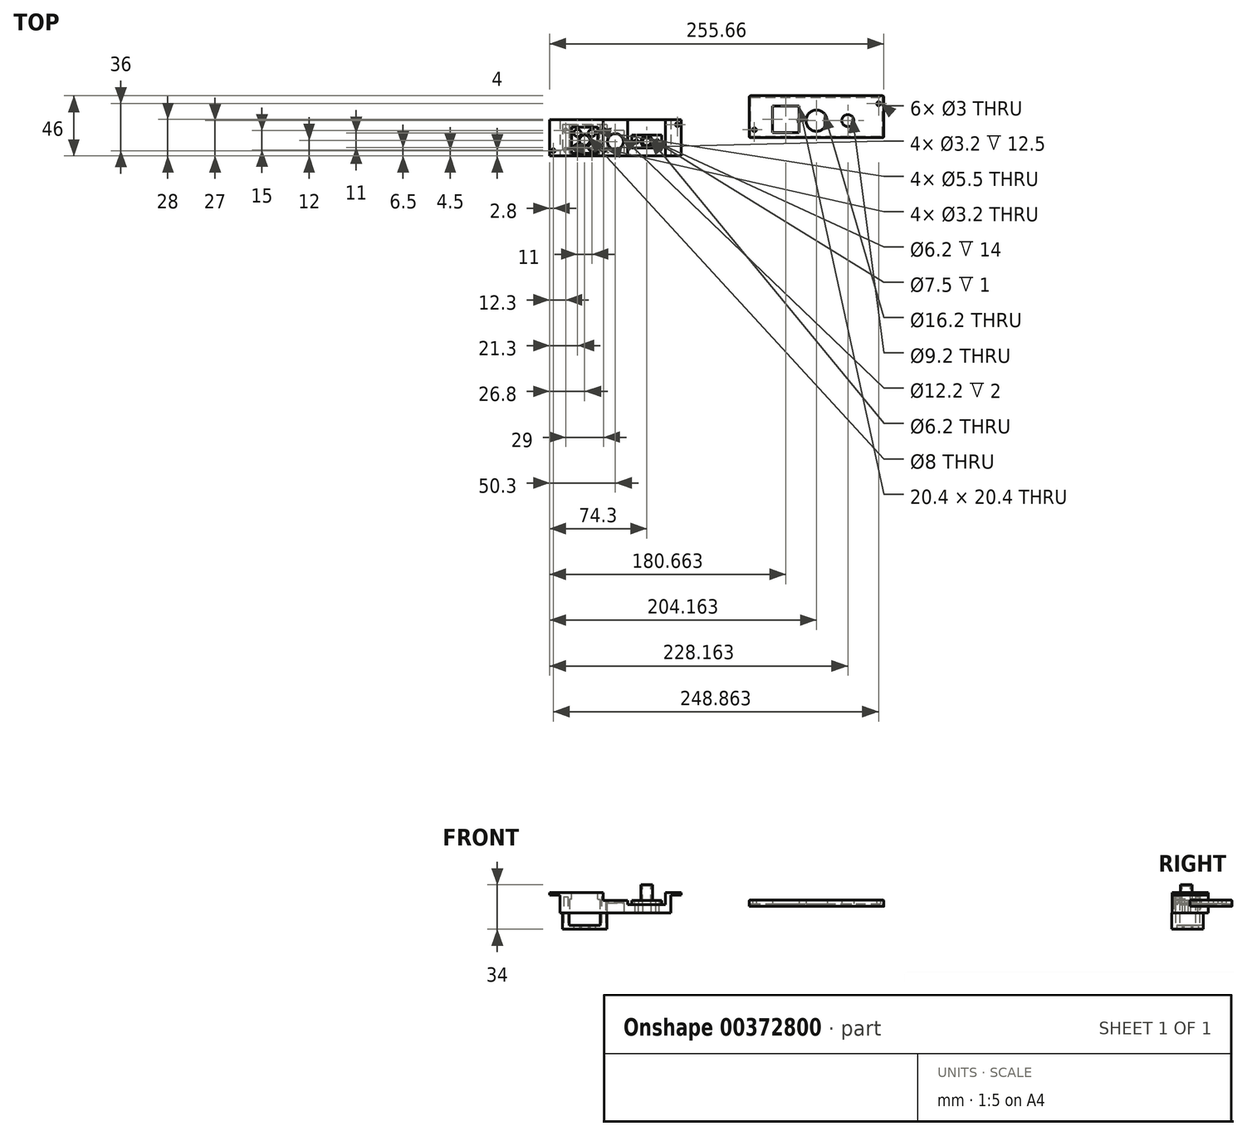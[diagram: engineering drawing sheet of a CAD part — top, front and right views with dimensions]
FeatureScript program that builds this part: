
annotation { "Feature Type Name" : "Feature", "Feature Type Description" : "" }
export const myFeature = defineFeature(function(context is Context, id is Id, definition is map)
    precondition{}
    {
        {
            var Q0;
            Q0=qCreatedBy(makeId("Top.planeOp"),FACE);
            var sketch = newSketch(context, id + "F0", { "sketchPlane" : qUnion([Q0])});
            skPoint(sketch, "E0.middle", {"position": v(0, 0) * mm});
            skCircle(sketch, "E1", {"center": v(-47.5, -10) * mm, "radius": 1.3 * mm, "construction": true});
            skCircle(sketch, "E2", {"center": v(47.5, 10) * mm, "radius": 1.3 * mm, "construction": true});
            skLineSegment(sketch, "E3.bottom", {"start": v(-32.5, 7) * mm, "end": v(-14.5, 7) * mm, "construction": true});
            skLineSegment(sketch, "E3.top", {"start": v(-32.5, -11) * mm, "end": v(-14.5, -11) * mm, "construction": true});
            skLineSegment(sketch, "E3.left", {"start": v(-32.5, 7) * mm, "end": v(-32.5, -1) * mm, "construction": true});
            skLineSegment(sketch, "E3.right", {"start": v(-14.5, 7) * mm, "end": v(-14.5, -11) * mm, "construction": true});
            skLineSegment(sketch, "E4.bottom", {"start": v(-29.25, 7) * mm, "end": v(-27.25, 7) * mm, "construction": true});
            skLineSegment(sketch, "E4.top", {"start": v(-29.25, -11) * mm, "end": v(-27.25, -11) * mm, "construction": true});
            skLineSegment(sketch, "E4.left", {"start": v(-29.25, 7) * mm, "end": v(-29.25, -1) * mm, "construction": true});
            skLineSegment(sketch, "E4.right", {"start": v(-27.25, 7) * mm, "end": v(-27.25, -1) * mm, "construction": true});
            skLineSegment(sketch, "E5.bottom", {"start": v(-19.75, 7) * mm, "end": v(-17.75, 7) * mm, "construction": true});
            skLineSegment(sketch, "E5.top", {"start": v(-19.75, -11) * mm, "end": v(-17.75, -11) * mm, "construction": true});
            skLineSegment(sketch, "E5.left", {"start": v(-19.75, 7) * mm, "end": v(-19.75, -1) * mm, "construction": true});
            skLineSegment(sketch, "E5.right", {"start": v(-17.75, 7) * mm, "end": v(-17.75, -1) * mm, "construction": true});
            skLineSegment(sketch, "E6.bottom", {"start": v(-32.5, -1) * mm, "end": v(-29.25, -1) * mm, "construction": true});
            skLineSegment(sketch, "E6.top", {"start": v(-32.5, -3) * mm, "end": v(-29.25, -3) * mm, "construction": true});
            skLineSegment(sketch, "E6.left", {"start": v(-32.5, -1) * mm, "end": v(-32.5, -3) * mm, "construction": true});
            skLineSegment(sketch, "E7.trimOffspring", {"start": v(-29.25, -3) * mm, "end": v(-29.25, -11) * mm, "construction": true});
            skLineSegment(sketch, "E8.trimOffspring", {"start": v(-27.25, -1) * mm, "end": v(-19.75, -1) * mm, "construction": true});
            skLineSegment(sketch, "E9.trimOffspring", {"start": v(-27.25, -3) * mm, "end": v(-27.25, -11) * mm, "construction": true});
            skLineSegment(sketch, "E10.trimOffspring", {"start": v(-27.25, -3) * mm, "end": v(-19.75, -3) * mm, "construction": true});
            skLineSegment(sketch, "E11.trimOffspring", {"start": v(-17.75, -1) * mm, "end": v(-14.5, -1) * mm, "construction": true});
            skLineSegment(sketch, "E12.trimOffspring", {"start": v(-17.75, -3) * mm, "end": v(-14.5, -3) * mm, "construction": true});
            skLineSegment(sketch, "E13.trimOffspring", {"start": v(-19.75, -3) * mm, "end": v(-19.75, -11) * mm, "construction": true});
            skLineSegment(sketch, "E14.trimOffspring", {"start": v(-17.75, -3) * mm, "end": v(-17.75, -11) * mm, "construction": true});
            skLineSegment(sketch, "E15.trimOffspring", {"start": v(-32.5, -3) * mm, "end": v(-32.5, -11) * mm, "construction": true});
            skCircle(sketch, "E16", {"center": v(24, -3) * mm, "radius": 3.1 * mm});
            skLineSegment(sketch, "E17.bottom", {"start": v(22.75, -10.5) * mm, "end": v(20.75, -10.5) * mm, "construction": true});
            skLineSegment(sketch, "E17.top", {"start": v(22.75, 4.5) * mm, "end": v(20.75, 4.5) * mm, "construction": true});
            skLineSegment(sketch, "E17.left", {"start": v(22.75, -10.5) * mm, "end": v(22.75, 4.5) * mm, "construction": true});
            skLineSegment(sketch, "E17.right", {"start": v(20.75, -10.5) * mm, "end": v(20.75, 4.5) * mm, "construction": true});
            skPoint(sketch, "E17.middle", {"position": v(21.75, -3) * mm});
            skLineSegment(sketch, "E18.bottom", {"start": v(25.25, -10.5) * mm, "end": v(27.25, -10.5) * mm, "construction": true});
            skLineSegment(sketch, "E18.top", {"start": v(25.25, 4.5) * mm, "end": v(27.25, 4.5) * mm, "construction": true});
            skLineSegment(sketch, "E18.left", {"start": v(25.25, -10.5) * mm, "end": v(25.25, 4.5) * mm, "construction": true});
            skLineSegment(sketch, "E18.right", {"start": v(27.25, -10.5) * mm, "end": v(27.25, 4.5) * mm, "construction": true});
            skPoint(sketch, "E18.middle", {"position": v(26.25, -3) * mm});
            skCircle(sketch, "E19", {"center": v(16, -3) * mm, "radius": 1.2 * mm});
            skPoint(sketch, "E19.centerSnap0", {"position": v(20.75, -3) * mm});
            skCircle(sketch, "E20", {"center": v(32, -3) * mm, "radius": 1.2 * mm});
            skPoint(sketch, "E20.centerSnap0", {"position": v(27.25, -3) * mm});
            skLineSegment(sketch, "E21.bottom", {"start": v(42.3, -13.8) * mm, "end": v(-42.3, -13.8) * mm});
            skLineSegment(sketch, "E21.top", {"start": v(42.3, 13.8) * mm, "end": v(-42.3, 13.8) * mm});
            skLineSegment(sketch, "E21.left", {"start": v(42.3, -13.8) * mm, "end": v(42.3, 13.8) * mm});
            skLineSegment(sketch, "E21.right", {"start": v(-42.3, -13.8) * mm, "end": v(-42.3, 13.8) * mm});
            skLineSegment(sketch, "E22.bottom", {"start": v(50.5, -15) * mm, "end": v(-50.5, -15) * mm, "construction": true});
            skLineSegment(sketch, "E22.top", {"start": v(50.5, 15) * mm, "end": v(-50.5, 15) * mm, "construction": true});
            skLineSegment(sketch, "E22.left", {"start": v(50.5, -15) * mm, "end": v(50.5, 15) * mm, "construction": true});
            skLineSegment(sketch, "E22.right", {"start": v(-50.5, -15) * mm, "end": v(-50.5, 15) * mm, "construction": true});
            skCircle(sketch, "E23", {"center": v(0, -3) * mm, "radius": 6.1 * mm, "construction": true});
            skSolve(sketch);
        }
        {
            var Q0;
            Q0 = qSketchRegion(id + "F0", true);
            extrude(context, id + "F1", {"entities" : qUnion([Q0]), "depth" : 1.5 * mm, "offsetDistance" : 25 * mm});
        }
        {
            var Q0;
            Q0=qCreatedBy(makeId("Top.planeOp"),FACE);
            var sketch = newSketch(context, id + "F2", { "sketchPlane" : qUnion([Q0])});
            skLineSegment(sketch, "E24.bottom", {"start": v(103.36, 32) * mm, "end": v(204.36, 32) * mm, "construction": true});
            skLineSegment(sketch, "E24.top", {"start": v(103.36, 0) * mm, "end": v(204.36, 0) * mm, "construction": true});
            skLineSegment(sketch, "E24.left", {"start": v(103.36, 32) * mm, "end": v(103.36, 0) * mm, "construction": true});
            skLineSegment(sketch, "E24.right", {"start": v(204.36, 32) * mm, "end": v(204.36, 0) * mm, "construction": true});
            skLineSegment(sketch, "E25.bottom", {"start": v(102.36, 32) * mm, "end": v(205.36, 32) * mm});
            skLineSegment(sketch, "E25.top", {"start": v(102.36, 0) * mm, "end": v(205.36, 0) * mm});
            skLineSegment(sketch, "E25.left", {"start": v(102.36, 32) * mm, "end": v(102.36, 0) * mm});
            skLineSegment(sketch, "E25.right", {"start": v(205.36, 32) * mm, "end": v(205.36, 0) * mm});
            skCircle(sketch, "E26", {"center": v(106.36, 6) * mm, "radius": 1.5 * mm});
            skCircle(sketch, "E27", {"center": v(201.36, 26) * mm, "radius": 1.5 * mm});
            skCircle(sketch, "E28", {"center": v(153.86, 13) * mm, "radius": 8.1 * mm});
            skCircle(sketch, "E29", {"center": v(177.86, 13) * mm, "radius": 4.6 * mm});
            skLineSegment(sketch, "E30.bottom", {"start": v(140.56, 3.8) * mm, "end": v(120.16, 3.8) * mm});
            skLineSegment(sketch, "E30.top", {"start": v(140.56, 24.2) * mm, "end": v(120.16, 24.2) * mm});
            skLineSegment(sketch, "E30.left", {"start": v(140.56, 3.8) * mm, "end": v(140.56, 24.2) * mm});
            skLineSegment(sketch, "E30.right", {"start": v(120.16, 3.8) * mm, "end": v(120.16, 24.2) * mm});
            skPoint(sketch, "E30.middle", {"position": v(130.36, 14) * mm});
            skSolve(sketch);
        }
        {
            var Q0;
            Q0=qSketchRegion(id+"F2",true);
            extrude(context, id + "F3", {"entities" : qUnion([Q0]), "depth" : 5 * mm});
        }
        {
            var Q0;
            Q0=makeQuery(id+"F3.opExtrude","CAP_FACE",FACE,{"disambiguationData":[OSD([sQuery(id+"F2.wireOp",EDGE,"E25.bottom"),sQuery(id+"F2.wireOp",EDGE,"E25.top"),sQuery(id+"F2.wireOp",EDGE,"E25.left"),sQuery(id+"F2.wireOp",EDGE,"E25.right"),sQuery(id+"F2.wireOp",EDGE,"E26"),sQuery(id+"F2.wireOp",EDGE,"E27"),sQuery(id+"F2.wireOp",EDGE,"RyGLUrYX-1u43-e16M-MsOJ-A2O3aQofN9jR.bottom"),sQuery(id+"F2.wireOp",EDGE,"RyGLUrYX-1u43-e16M-MsOJ-A2O3aQofN9jR.top"),sQuery(id+"F2.wireOp",EDGE,"RyGLUrYX-1u43-e16M-MsOJ-A2O3aQofN9jR.left"),sQuery(id+"F2.wireOp",EDGE,"RyGLUrYX-1u43-e16M-MsOJ-A2O3aQofN9jR.right")])],"isStart":true});
            var sketch = newSketch(context, id + "F4", { "sketchPlane" : qUnion([Q0])});
            skLineSegment(sketch, "E31.bottom", {"start": v(103.36, -1) * mm, "end": v(204.36, -1) * mm});
            skLineSegment(sketch, "E31.top", {"start": v(103.36, -31) * mm, "end": v(204.36, -31) * mm});
            skLineSegment(sketch, "E31.left", {"start": v(103.36, -1) * mm, "end": v(103.36, -31) * mm});
            skLineSegment(sketch, "E31.right", {"start": v(204.36, -1) * mm, "end": v(204.36, -31) * mm});
            skSolve(sketch);
        }
        {
            var Q0;
            Q0=qSketchRegion(id+"F4",true);
            extrude(context, id + "F5", {"entities" : qUnion([Q0]), "operationType" : NewBodyOperationType.REMOVE, "oppositeDirection" : true, "depth" : 2 * mm});
        }
        {
            var Q0;
            Q0=makeQuery(id+"F3.opExtrude","CAP_EDGE",EDGE,{"disambiguationData":[OSD([sQuery(id+"F2.wireOp",EDGE,"E25.left")])],"isStart":false});
            var Q1;
            Q1=makeQuery(id+"F3.opExtrude","CAP_EDGE",EDGE,{"disambiguationData":[OSD([sQuery(id+"F2.wireOp",EDGE,"E25.bottom")])],"isStart":false});
            var Q2;
            Q2=makeQuery(id+"F3.opExtrude","CAP_EDGE",EDGE,{"disambiguationData":[OSD([sQuery(id+"F2.wireOp",EDGE,"E25.top")])],"isStart":false});
            var Q3;
            Q3=makeQuery(id+"F3.opExtrude","CAP_EDGE",EDGE,{"disambiguationData":[OSD([sQuery(id+"F2.wireOp",EDGE,"E25.right")])],"isStart":false});
            var Q4;
            Q4=makeQuery(id+"F3.opExtrude","SWEPT_EDGE",EDGE,{"disambiguationData":[OSD([sQuery(id+"F2.wireOp",EDGE,"E25.bottom"),sQuery(id+"F2.wireOp",EDGE,"E25.right")])]});
            var Q5;
            Q5=makeQuery(id+"F3.opExtrude","SWEPT_EDGE",EDGE,{"disambiguationData":[OSD([sQuery(id+"F2.wireOp",EDGE,"E25.top"),sQuery(id+"F2.wireOp",EDGE,"E25.right")])]});
            var Q6;
            Q6=makeQuery(id+"F3.opExtrude","SWEPT_EDGE",EDGE,{"disambiguationData":[OSD([sQuery(id+"F2.wireOp",EDGE,"E25.bottom"),sQuery(id+"F2.wireOp",EDGE,"E25.left")])]});
            var Q7;
            Q7=makeQuery(id+"F3.opExtrude","SWEPT_EDGE",EDGE,{"disambiguationData":[OSD([sQuery(id+"F2.wireOp",EDGE,"E25.top"),sQuery(id+"F2.wireOp",EDGE,"E25.left")])]});
            fillet(context, id + "F6", {"entities" : qUnion([Q0, Q1, Q2, Q3, Q4, Q5, Q6, Q7]), "radius" : 1 * mm, "tangentPropagation" : true, "allowEdgeOverflow" : false});
        }
        {
            var Q0;
            Q0=makeQuery(id+"F1.opExtrude","SWEPT_FACE",FACE,{"disambiguationData":[OSD([sQuery(id+"F0.wireOp",EDGE,"E21.bottom")])]});
            var sketch = newSketch(context, id + "F7", { "sketchPlane" : qUnion([Q0])});
            skLineSegment(sketch, "E32.bottom", {"start": v(-42.3, 1.5) * mm, "end": v(-40.3, 1.5) * mm});
            skLineSegment(sketch, "E32.left", {"start": v(-42.3, 1.5) * mm, "end": v(-42.3, 8.5) * mm});
            skLineSegment(sketch, "E32.right", {"start": v(-40.3, 1.5) * mm, "end": v(-40.3, 10.5) * mm});
            skLineSegment(sketch, "E33.bottom", {"start": v(-40.3, 10.5) * mm, "end": v(-50.3, 10.5) * mm});
            skLineSegment(sketch, "E33.top", {"start": v(-42.3, 8.5) * mm, "end": v(-50.3, 8.5) * mm});
            skLineSegment(sketch, "E33.right", {"start": v(-50.3, 10.5) * mm, "end": v(-50.3, 8.5) * mm});
            skLineSegment(sketch, "E34", {"start": v(0, 8.22) * mm, "end": v(0, -6.23) * mm, "construction": true});
            skPoint(sketch, "E34.endSnap0", {"position": v(0, 1.5) * mm});
            skLineSegment(sketch, "E35.MirrorCS", {"start": v(42.3, 10.5) * mm, "end": v(40.3, 10.5) * mm});
            skLineSegment(sketch, "E36.MirrorCS", {"start": v(42.3, 10.5) * mm, "end": v(42.3, 8.5) * mm});
            skLineSegment(sketch, "E37.MirrorCS", {"start": v(42.3, 1.5) * mm, "end": v(40.3, 1.5) * mm});
            skLineSegment(sketch, "E38.MirrorCS", {"start": v(40.3, 1.5) * mm, "end": v(40.3, 10.5) * mm});
            skLineSegment(sketch, "E39.MirrorCS", {"start": v(50.3, 10.5) * mm, "end": v(50.3, 8.5) * mm});
            skLineSegment(sketch, "E40.MirrorCS", {"start": v(42.3, 1.5) * mm, "end": v(42.3, 10.5) * mm});
            skLineSegment(sketch, "E41.MirrorCS", {"start": v(42.3, 10.5) * mm, "end": v(50.3, 10.5) * mm});
            skLineSegment(sketch, "E42.MirrorCS", {"start": v(42.3, 8.5) * mm, "end": v(50.3, 8.5) * mm});
            skSolve(sketch);
        }
        {
            var Q0;
            Q0 = qSketchRegion(id + "F7", true);
            extrude(context, id + "F8", {"entities" : qUnion([Q0]), "operationType" : NewBodyOperationType.ADD, "oppositeDirection" : true, "depth" : 27.6 * mm});
        }
        {
            var Q0;
            Q0=sQuery(id+"F0.wireOp",VERTEX,"E1.center");
            var Q1;
            Q1=sQuery(id+"F0.wireOp",VERTEX,"E2.center");
            var Q2;
            Q2=makeQuery(id+"F1.opExtrude","SWEPT_BODY",BODY,{"disambiguationData":[OSD([sQuery(id+"F0.wireOp",EDGE,"E3.bottom"),sQuery(id+"F0.wireOp",EDGE,"E3.top"),sQuery(id+"F0.wireOp",EDGE,"E3.left"),sQuery(id+"F0.wireOp",EDGE,"E3.right"),sQuery(id+"F0.wireOp",EDGE,"E4.left"),sQuery(id+"F0.wireOp",EDGE,"E4.right"),sQuery(id+"F0.wireOp",EDGE,"E5.left"),sQuery(id+"F0.wireOp",EDGE,"E5.right"),sQuery(id+"F0.wireOp",EDGE,"E6.bottom"),sQuery(id+"F0.wireOp",EDGE,"E6.top"),sQuery(id+"F0.wireOp",EDGE,"E7.trimOffspring"),sQuery(id+"F0.wireOp",EDGE,"E8.trimOffspring"),sQuery(id+"F0.wireOp",EDGE,"E9.trimOffspring"),sQuery(id+"F0.wireOp",EDGE,"E10.trimOffspring"),sQuery(id+"F0.wireOp",EDGE,"E11.trimOffspring"),sQuery(id+"F0.wireOp",EDGE,"E12.trimOffspring"),sQuery(id+"F0.wireOp",EDGE,"E13.trimOffspring"),sQuery(id+"F0.wireOp",EDGE,"E14.trimOffspring"),sQuery(id+"F0.wireOp",EDGE,"E15.trimOffspring"),sQuery(id+"F0.wireOp",EDGE,"E17.bottom"),sQuery(id+"F0.wireOp",EDGE,"E17.top"),sQuery(id+"F0.wireOp",EDGE,"E17.left"),sQuery(id+"F0.wireOp",EDGE,"E17.right"),sQuery(id+"F0.wireOp",EDGE,"E18.bottom"),sQuery(id+"F0.wireOp",EDGE,"E18.top"),sQuery(id+"F0.wireOp",EDGE,"E18.left"),sQuery(id+"F0.wireOp",EDGE,"E18.right"),sQuery(id+"F0.wireOp",EDGE,"E19"),sQuery(id+"F0.wireOp",EDGE,"E20"),sQuery(id+"F0.wireOp",EDGE,"E21.bottom"),sQuery(id+"F0.wireOp",EDGE,"E21.top"),sQuery(id+"F0.wireOp",EDGE,"E21.left"),sQuery(id+"F0.wireOp",EDGE,"E21.right"),sQuery(id+"F0.wireOp",EDGE,"P8dx2Xio-yyFz-oP8E-liUG-BQfSMQLC5rHF")])]});
            hole(context, id + "F9", {"style" : HoleStyle.SIMPLE, "endStyle" : HoleEndStyle.BLIND, "oppositeDirection" : true, "holeDiameter" : 3 * mm, "holeDepth" : 5 * mm, "tappedDepth" : 12 * mm, "tapClearance" : 3, "locations" : qUnion([Q0, Q1]), "scope" : qUnion([Q2])});
        }
        {
            var Q0;
            Q0=makeQuery(id+"F1.opExtrude","CAP_FACE",FACE,{"disambiguationData":[OSD([sQuery(id+"F0.wireOp",EDGE,"E3.bottom"),sQuery(id+"F0.wireOp",EDGE,"E3.top"),sQuery(id+"F0.wireOp",EDGE,"E3.left"),sQuery(id+"F0.wireOp",EDGE,"E3.right"),sQuery(id+"F0.wireOp",EDGE,"E4.left"),sQuery(id+"F0.wireOp",EDGE,"E4.right"),sQuery(id+"F0.wireOp",EDGE,"E5.left"),sQuery(id+"F0.wireOp",EDGE,"E5.right"),sQuery(id+"F0.wireOp",EDGE,"E6.bottom"),sQuery(id+"F0.wireOp",EDGE,"E6.top"),sQuery(id+"F0.wireOp",EDGE,"E7.trimOffspring"),sQuery(id+"F0.wireOp",EDGE,"E8.trimOffspring"),sQuery(id+"F0.wireOp",EDGE,"E9.trimOffspring"),sQuery(id+"F0.wireOp",EDGE,"E10.trimOffspring"),sQuery(id+"F0.wireOp",EDGE,"E11.trimOffspring"),sQuery(id+"F0.wireOp",EDGE,"E12.trimOffspring"),sQuery(id+"F0.wireOp",EDGE,"E13.trimOffspring"),sQuery(id+"F0.wireOp",EDGE,"E14.trimOffspring"),sQuery(id+"F0.wireOp",EDGE,"E15.trimOffspring"),sQuery(id+"F0.wireOp",EDGE,"E17.bottom"),sQuery(id+"F0.wireOp",EDGE,"E17.top"),sQuery(id+"F0.wireOp",EDGE,"E17.left"),sQuery(id+"F0.wireOp",EDGE,"E17.right"),sQuery(id+"F0.wireOp",EDGE,"E18.bottom"),sQuery(id+"F0.wireOp",EDGE,"E18.top"),sQuery(id+"F0.wireOp",EDGE,"E18.left"),sQuery(id+"F0.wireOp",EDGE,"E18.right"),sQuery(id+"F0.wireOp",EDGE,"E19"),sQuery(id+"F0.wireOp",EDGE,"E20"),sQuery(id+"F0.wireOp",EDGE,"E21.bottom"),sQuery(id+"F0.wireOp",EDGE,"E21.top"),sQuery(id+"F0.wireOp",EDGE,"E21.left"),sQuery(id+"F0.wireOp",EDGE,"E21.right"),sQuery(id+"F0.wireOp",EDGE,"P8dx2Xio-yyFz-oP8E-liUG-BQfSMQLC5rHF")])],"isStart":false});
            var sketch = newSketch(context, id + "F10", { "sketchPlane" : qUnion([Q0])});
            skLineSegment(sketch, "E43.bottom", {"start": v(35.5, -8) * mm, "end": v(12.5, -8) * mm});
            skLineSegment(sketch, "E43.top", {"start": v(35.5, 2) * mm, "end": v(12.5, 2) * mm});
            skLineSegment(sketch, "E43.left", {"start": v(35.5, -8) * mm, "end": v(35.5, 2) * mm});
            skLineSegment(sketch, "E43.right", {"start": v(12.5, -8) * mm, "end": v(12.5, 2) * mm});
            skPoint(sketch, "E43.middle", {"position": v(24, -3) * mm});
            skCircle(sketch, "E44", {"center": v(16, -3) * mm, "radius": 1.5 * mm});
            skCircle(sketch, "E45", {"center": v(32, -3) * mm, "radius": 1.5 * mm});
            skSolve(sketch);
        }
        {
            var Q0;
            Q0 = qSketchRegion(id + "F10", true);
            extrude(context, id + "F11", {"entities" : qUnion([Q0]), "depth" : 3 * mm});
        }
        {
            var Q0;
            Q0=makeQuery(id+"F11.opExtrude","CAP_FACE",FACE,{"disambiguationData":[OSD([sQuery(id+"F10.wireOp",EDGE,"E43.bottom"),sQuery(id+"F10.wireOp",EDGE,"E43.top"),sQuery(id+"F10.wireOp",EDGE,"E43.left"),sQuery(id+"F10.wireOp",EDGE,"E43.right"),sQuery(id+"F10.wireOp",EDGE,"E44"),sQuery(id+"F10.wireOp",EDGE,"E45")])],"isStart":false});
            var sketch = newSketch(context, id + "F12", { "sketchPlane" : qUnion([Q0])});
            skCircle(sketch, "E46", {"center": v(24, -3) * mm, "radius": 4.5 * mm});
            skPoint(sketch, "E46.centerSnap0", {"position": v(24, 2) * mm});
            skPoint(sketch, "E46.centerSnap1", {"position": v(35.5, -3) * mm});
            skSolve(sketch);
        }
        {
            var Q0;
            Q0 = qSketchRegion(id + "F12", true);
            extrude(context, id + "F13", {"entities" : qUnion([Q0]), "operationType" : NewBodyOperationType.ADD, "depth" : 12 * mm});
        }
        {
            var Q0;
            Q0=makeQuery(id+"F13.opExtrude","CAP_FACE",FACE,{"disambiguationData":[OSD([sQuery(id+"F12.wireOp",EDGE,"E46")])],"isStart":false});
            var sketch = newSketch(context, id + "F14", { "sketchPlane" : qUnion([Q0])});
            skCircle(sketch, "E47", {"center": v(24, -3) * mm, "radius": 3.1 * mm});
            skSolve(sketch);
        }
        {
            var Q0;
            Q0 = qSketchRegion(id + "F14", true);
            extrude(context, id + "F15", {"entities" : qUnion([Q0]), "operationType" : NewBodyOperationType.REMOVE, "oppositeDirection" : true, "depth" : 25 * mm});
        }
        {
            var Q0;
            Q0=makeQuery(id+"F1.opExtrude","CAP_FACE",FACE,{"disambiguationData":[OSD([sQuery(id+"F0.wireOp",EDGE,"E3.bottom"),sQuery(id+"F0.wireOp",EDGE,"E3.top"),sQuery(id+"F0.wireOp",EDGE,"E3.left"),sQuery(id+"F0.wireOp",EDGE,"E3.right"),sQuery(id+"F0.wireOp",EDGE,"E4.left"),sQuery(id+"F0.wireOp",EDGE,"E4.right"),sQuery(id+"F0.wireOp",EDGE,"E5.left"),sQuery(id+"F0.wireOp",EDGE,"E5.right"),sQuery(id+"F0.wireOp",EDGE,"E6.bottom"),sQuery(id+"F0.wireOp",EDGE,"E6.top"),sQuery(id+"F0.wireOp",EDGE,"E7.trimOffspring"),sQuery(id+"F0.wireOp",EDGE,"E8.trimOffspring"),sQuery(id+"F0.wireOp",EDGE,"E9.trimOffspring"),sQuery(id+"F0.wireOp",EDGE,"E10.trimOffspring"),sQuery(id+"F0.wireOp",EDGE,"E11.trimOffspring"),sQuery(id+"F0.wireOp",EDGE,"E12.trimOffspring"),sQuery(id+"F0.wireOp",EDGE,"E13.trimOffspring"),sQuery(id+"F0.wireOp",EDGE,"E14.trimOffspring"),sQuery(id+"F0.wireOp",EDGE,"E15.trimOffspring"),sQuery(id+"F0.wireOp",EDGE,"E17.bottom"),sQuery(id+"F0.wireOp",EDGE,"E17.top"),sQuery(id+"F0.wireOp",EDGE,"E17.left"),sQuery(id+"F0.wireOp",EDGE,"E17.right"),sQuery(id+"F0.wireOp",EDGE,"E18.bottom"),sQuery(id+"F0.wireOp",EDGE,"E18.top"),sQuery(id+"F0.wireOp",EDGE,"E18.left"),sQuery(id+"F0.wireOp",EDGE,"E18.right"),sQuery(id+"F0.wireOp",EDGE,"E19"),sQuery(id+"F0.wireOp",EDGE,"E20"),sQuery(id+"F0.wireOp",EDGE,"E21.bottom"),sQuery(id+"F0.wireOp",EDGE,"E21.top"),sQuery(id+"F0.wireOp",EDGE,"E21.left"),sQuery(id+"F0.wireOp",EDGE,"E21.right")])],"isStart":false});
            var sketch = newSketch(context, id + "F16", { "sketchPlane" : qUnion([Q0])});
            skLineSegment(sketch, "E48.bottom", {"start": v(-9.5, 13.8) * mm, "end": v(9.5, 13.8) * mm});
            skLineSegment(sketch, "E48.top", {"start": v(-9.5, -13.8) * mm, "end": v(9.5, -13.8) * mm});
            skLineSegment(sketch, "E48.left", {"start": v(-9.5, 13.8) * mm, "end": v(-9.5, -13.8) * mm});
            skLineSegment(sketch, "E48.right", {"start": v(9.5, 13.8) * mm, "end": v(9.5, -13.8) * mm});
            skSolve(sketch);
        }
        {
            var Q0;
            Q0 = qSketchRegion(id + "F16", true);
            extrude(context, id + "F17", {"entities" : qUnion([Q0]), "operationType" : NewBodyOperationType.ADD, "depth" : 3 * mm});
        }
        {
            var Q0;
            Q0=sQuery(id+"F0.wireOp",VERTEX,"E23.center");
            var Q1;
            Q1=makeQuery(id+"F1.opExtrude","SWEPT_BODY",BODY,{"disambiguationData":[OSD([sQuery(id+"F0.wireOp",EDGE,"E3.bottom"),sQuery(id+"F0.wireOp",EDGE,"E3.top"),sQuery(id+"F0.wireOp",EDGE,"E3.left"),sQuery(id+"F0.wireOp",EDGE,"E3.right"),sQuery(id+"F0.wireOp",EDGE,"E4.left"),sQuery(id+"F0.wireOp",EDGE,"E4.right"),sQuery(id+"F0.wireOp",EDGE,"E5.left"),sQuery(id+"F0.wireOp",EDGE,"E5.right"),sQuery(id+"F0.wireOp",EDGE,"E6.bottom"),sQuery(id+"F0.wireOp",EDGE,"E6.top"),sQuery(id+"F0.wireOp",EDGE,"E7.trimOffspring"),sQuery(id+"F0.wireOp",EDGE,"E8.trimOffspring"),sQuery(id+"F0.wireOp",EDGE,"E9.trimOffspring"),sQuery(id+"F0.wireOp",EDGE,"E10.trimOffspring"),sQuery(id+"F0.wireOp",EDGE,"E11.trimOffspring"),sQuery(id+"F0.wireOp",EDGE,"E12.trimOffspring"),sQuery(id+"F0.wireOp",EDGE,"E13.trimOffspring"),sQuery(id+"F0.wireOp",EDGE,"E14.trimOffspring"),sQuery(id+"F0.wireOp",EDGE,"E15.trimOffspring"),sQuery(id+"F0.wireOp",EDGE,"E17.bottom"),sQuery(id+"F0.wireOp",EDGE,"E17.top"),sQuery(id+"F0.wireOp",EDGE,"E17.left"),sQuery(id+"F0.wireOp",EDGE,"E17.right"),sQuery(id+"F0.wireOp",EDGE,"E18.bottom"),sQuery(id+"F0.wireOp",EDGE,"E18.top"),sQuery(id+"F0.wireOp",EDGE,"E18.left"),sQuery(id+"F0.wireOp",EDGE,"E18.right"),sQuery(id+"F0.wireOp",EDGE,"E19"),sQuery(id+"F0.wireOp",EDGE,"E20"),sQuery(id+"F0.wireOp",EDGE,"E21.bottom"),sQuery(id+"F0.wireOp",EDGE,"E21.top"),sQuery(id+"F0.wireOp",EDGE,"E21.left"),sQuery(id+"F0.wireOp",EDGE,"E21.right")])]});
            hole(context, id + "F18", {"style" : HoleStyle.SIMPLE, "endStyle" : HoleEndStyle.BLIND, "oppositeDirection" : true, "holeDiameter" : 12.2 * mm, "holeDepth" : 5 * mm, "tappedDepth" : 12 * mm, "tapClearance" : 3, "locations" : qUnion([Q0]), "scope" : qUnion([Q1]), "majorDiameter" : 5 * mm});
        }
        {
            var Q0;
            Q0=makeQuery(id+"F13.opExtrude","CAP_FACE",FACE,{"disambiguationData":[OSD([sQuery(id+"F12.wireOp",EDGE,"E46")])],"isStart":false});
            var sketch = newSketch(context, id + "F19", { "sketchPlane" : qUnion([Q0])});
            skCircle(sketch, "E49", {"center": v(24, -3) * mm, "radius": 3.75 * mm});
            skSolve(sketch);
        }
        {
            var Q0;
            Q0 = qSketchRegion(id + "F19", true);
            extrude(context, id + "F20", {"entities" : qUnion([Q0]), "operationType" : NewBodyOperationType.REMOVE, "oppositeDirection" : true, "depth" : 1 * mm});
        }
        {
            var Q0;
            Q0=makeQuery(id+"F17.boolean.opBoolean","MERGE",FACE,{"derivedFrom":[makeQuery(id+"F8.boolean.opBoolean","MERGE",FACE,{"derivedFrom":[makeQuery(id+"F1.opExtrude","SWEPT_FACE",FACE,{"disambiguationData":[OSD([sQuery(id+"F0.wireOp",EDGE,"E21.bottom")])]}),makeQuery(id+"F8.opExtrude","CAP_FACE",FACE,{"disambiguationData":[OSD([sQuery(id+"F7.wireOp",EDGE,"E32.bottom"),sQuery(id+"F7.wireOp",EDGE,"E32.left"),sQuery(id+"F7.wireOp",EDGE,"E32.right"),sQuery(id+"F7.wireOp",EDGE,"E33.bottom"),sQuery(id+"F7.wireOp",EDGE,"E33.top"),sQuery(id+"F7.wireOp",EDGE,"E33.right")])],"isStart":true}),makeQuery(id+"F8.opExtrude","CAP_FACE",FACE,{"disambiguationData":[OSD([sQuery(id+"F7.wireOp",EDGE,"E35.MirrorCS"),sQuery(id+"F7.wireOp",EDGE,"E37.MirrorCS"),sQuery(id+"F7.wireOp",EDGE,"E38.MirrorCS"),sQuery(id+"F7.wireOp",EDGE,"E39.MirrorCS"),sQuery(id+"F7.wireOp",EDGE,"E40.MirrorCS"),sQuery(id+"F7.wireOp",EDGE,"E41.MirrorCS"),sQuery(id+"F7.wireOp",EDGE,"E42.MirrorCS")])],"isStart":true})]}),makeQuery(id+"F17.opExtrude","SWEPT_FACE",FACE,{"disambiguationData":[OSD([sQuery(id+"F16.wireOp",EDGE,"E48.top")])]})]});
            var sketch = newSketch(context, id + "F21", { "sketchPlane" : qUnion([Q0])});
            skPoint(sketch, "E50.oppositeSnap0", {"position": v(-9.5, 3) * mm});
            skLineSegment(sketch, "E50.bottom", {"start": v(-40.3, 1.5) * mm, "end": v(-9.5, 1.5) * mm});
            skLineSegment(sketch, "E50.top", {"start": v(-40.3, 10.5) * mm, "end": v(-9.5, 10.5) * mm});
            skLineSegment(sketch, "E50.left", {"start": v(-40.3, 1.5) * mm, "end": v(-40.3, 10.5) * mm});
            skLineSegment(sketch, "E50.right", {"start": v(-9.5, 1.5) * mm, "end": v(-9.5, 10.5) * mm});
            skLineSegment(sketch, "E51.bottom", {"start": v(40.3, 10.5) * mm, "end": v(38.3, 10.5) * mm});
            skLineSegment(sketch, "E51.top", {"start": v(40.3, 1.5) * mm, "end": v(38.3, 1.5) * mm});
            skLineSegment(sketch, "E51.left", {"start": v(40.3, 10.5) * mm, "end": v(40.3, 1.5) * mm});
            skLineSegment(sketch, "E51.right", {"start": v(38.3, 10.5) * mm, "end": v(38.3, 1.5) * mm});
            skLineSegment(sketch, "E52.bottom", {"start": v(-42.3, 0) * mm, "end": v(42.3, 0) * mm});
            skLineSegment(sketch, "E52.top", {"start": v(-42.3, -5) * mm, "end": v(42.3, -5) * mm});
            skLineSegment(sketch, "E52.left", {"start": v(-42.3, 0) * mm, "end": v(-42.3, -5) * mm});
            skLineSegment(sketch, "E52.right", {"start": v(42.3, 0) * mm, "end": v(42.3, -5) * mm});
            skSolve(sketch);
        }
        {
            var Q0;
            Q0 = qSketchRegion(id + "F21", true);
            extrude(context, id + "F22", {"entities" : qUnion([Q0]), "operationType" : NewBodyOperationType.ADD, "oppositeDirection" : true, "depth" : 27.6 * mm, "offsetDistance" : 25 * mm});
        }
        {
            var Q0;
            Q0=makeQuery(id+"F22.boolean.opBoolean","MERGE",FACE,{"derivedFrom":[makeQuery(id+"F8.opExtrude","SWEPT_FACE",FACE,{"disambiguationData":[OSD([sQuery(id+"F7.wireOp",EDGE,"E33.bottom")])]}),makeQuery(id+"F22.opExtrude","SWEPT_FACE",FACE,{"disambiguationData":[OSD([sQuery(id+"F21.wireOp",EDGE,"E50.top")])]})]});
            var sketch = newSketch(context, id + "F23", { "sketchPlane" : qUnion([Q0])});
            skLineSegment(sketch, "E53.bottom", {"start": v(-13.5, -12) * mm, "end": v(-33.5, -12) * mm});
            skLineSegment(sketch, "E53.top", {"start": v(-13.5, 8) * mm, "end": v(-33.5, 8) * mm});
            skLineSegment(sketch, "E53.left", {"start": v(-13.5, -12) * mm, "end": v(-13.5, 8) * mm});
            skLineSegment(sketch, "E53.right", {"start": v(-33.5, -12) * mm, "end": v(-33.5, 8) * mm});
            skPoint(sketch, "E53.middle", {"position": v(-23.5, -2) * mm});
            skSolve(sketch);
        }
        {
            var Q0;
            Q0 = qSketchRegion(id + "F23", true);
            extrude(context, id + "F24", {"entities" : qUnion([Q0]), "operationType" : NewBodyOperationType.REMOVE, "oppositeDirection" : true, "depth" : 25 * mm, "offsetDistance" : 25 * mm});
        }
        {
            var Q0;
            Q0=makeQuery(id+"F22.opExtrude","SWEPT_FACE",FACE,{"disambiguationData":[OSD([sQuery(id+"F21.wireOp",EDGE,"E52.top")])]});
            var sketch = newSketch(context, id + "F25", { "sketchPlane" : qUnion([Q0])});
            skLineSegment(sketch, "E54.bottom", {"start": v(-33.5, 12) * mm, "end": v(-35, 12) * mm});
            skLineSegment(sketch, "E54.top", {"start": v(-33.5, -8) * mm, "end": v(-35, -8) * mm});
            skLineSegment(sketch, "E54.left", {"start": v(-33.5, 12) * mm, "end": v(-33.5, -8) * mm});
            skLineSegment(sketch, "E54.right", {"start": v(-35, 12) * mm, "end": v(-35, -8) * mm});
            skLineSegment(sketch, "E55.bottom", {"start": v(-13.5, 12) * mm, "end": v(-12, 12) * mm});
            skLineSegment(sketch, "E55.top", {"start": v(-13.5, -8) * mm, "end": v(-12, -8) * mm});
            skLineSegment(sketch, "E55.left", {"start": v(-13.5, 12) * mm, "end": v(-13.5, -8) * mm});
            skLineSegment(sketch, "E55.right", {"start": v(-12, 12) * mm, "end": v(-12, -8) * mm});
            skSolve(sketch);
        }
        {
            var Q0;
            Q0 = qSketchRegion(id + "F25", true);
            extrude(context, id + "F26", {"entities" : qUnion([Q0]), "operationType" : NewBodyOperationType.REMOVE, "oppositeDirection" : true, "depth" : 10.5 * mm, "offsetDistance" : 25 * mm});
        }
        {
            var Q0;
            Q0=makeQuery(id+"F22.opExtrude","SWEPT_FACE",FACE,{"disambiguationData":[OSD([sQuery(id+"F21.wireOp",EDGE,"E52.top")])]});
            var sketch = newSketch(context, id + "F27", { "sketchPlane" : qUnion([Q0])});
            skLineSegment(sketch, "E56.bottom", {"start": v(6.5, -5.5) * mm, "end": v(-6.5, -5.5) * mm});
            skLineSegment(sketch, "E56.top", {"start": v(6.5, 11.5) * mm, "end": v(-6.5, 11.5) * mm});
            skLineSegment(sketch, "E56.left", {"start": v(6.5, -5.5) * mm, "end": v(6.5, 11.5) * mm});
            skLineSegment(sketch, "E56.right", {"start": v(-6.5, -5.5) * mm, "end": v(-6.5, 11.5) * mm});
            skPoint(sketch, "E56.middle", {"position": v(0, 3) * mm});
            skSolve(sketch);
        }
        {
            var Q0;
            Q0 = qSketchRegion(id + "F27", true);
            extrude(context, id + "F28", {"entities" : qUnion([Q0]), "operationType" : NewBodyOperationType.REMOVE, "oppositeDirection" : true, "depth" : 7.5 * mm, "offsetDistance" : 25 * mm});
        }
        {
            var Q0;
            Q0=makeQuery(id+"F22.opExtrude","SWEPT_FACE",FACE,{"disambiguationData":[OSD([sQuery(id+"F21.wireOp",EDGE,"E52.top")])]});
            cPlane(context, id + "F29", {"entities" : qUnion([Q0]), "cplaneType" : CPlaneType.OFFSET, "offset" : 12.5 * mm, "width" : 150 * mm, "height" : 150 * mm});
        }
        {
            var Q0;
            Q0=qCreatedBy(id+"F29.planeOp",FACE);
            var sketch = newSketch(context, id + "F30", { "sketchPlane" : qUnion([Q0])});
            skLineSegment(sketch, "E57.bottom", {"start": v(-6.5, -10) * mm, "end": v(-40.5, -10) * mm});
            skLineSegment(sketch, "E57.top", {"start": v(-6.5, 14) * mm, "end": v(-40.5, 14) * mm});
            skLineSegment(sketch, "E57.left", {"start": v(-6.5, -10) * mm, "end": v(-6.5, 14) * mm});
            skLineSegment(sketch, "E57.right", {"start": v(-40.5, -10) * mm, "end": v(-40.5, 14) * mm});
            skPoint(sketch, "E57.middle", {"position": v(-23.5, 2) * mm});
            skSolve(sketch);
        }
        {
            var Q0;
            Q0 = qSketchRegion(id + "F30", true);
            extrude(context, id + "F31", {"entities" : qUnion([Q0]), "oppositeDirection" : true, "depth" : 12.5 * mm, "offsetDistance" : 25 * mm});
        }
        {
            var Q0;
            Q0=makeQuery(id+"F31.opExtrude","SWEPT_FACE",FACE,{"disambiguationData":[OSD([sQuery(id+"F30.wireOp",EDGE,"E57.top")])]});
            var sketch = newSketch(context, id + "F32", { "sketchPlane" : qUnion([Q0])});
            skLineSegment(sketch, "E58.bottom", {"start": v(-35.5, -5) * mm, "end": v(-11.5, -5) * mm});
            skLineSegment(sketch, "E58.top", {"start": v(-35.5, -14.5) * mm, "end": v(-11.5, -14.5) * mm});
            skLineSegment(sketch, "E58.left", {"start": v(-35.5, -5) * mm, "end": v(-35.5, -14.5) * mm});
            skLineSegment(sketch, "E58.right", {"start": v(-11.5, -5) * mm, "end": v(-11.5, -14.5) * mm});
            skSolve(sketch);
        }
        {
            var Q0;
            Q0 = qSketchRegion(id + "F32", true);
            extrude(context, id + "F33", {"entities" : qUnion([Q0]), "operationType" : NewBodyOperationType.REMOVE, "oppositeDirection" : true, "depth" : 25 * mm, "offsetDistance" : 25 * mm});
        }
        {
            var Q0;
            Q0=makeQuery(id+"F31.opExtrude","CAP_FACE",FACE,{"disambiguationData":[OSD([sQuery(id+"F30.wireOp",EDGE,"E57.bottom"),sQuery(id+"F30.wireOp",EDGE,"E57.top"),sQuery(id+"F30.wireOp",EDGE,"E57.left"),sQuery(id+"F30.wireOp",EDGE,"E57.right")])],"isStart":true});
            var sketch = newSketch(context, id + "F34", { "sketchPlane" : qUnion([Q0])});
            skCircle(sketch, "E59", {"center": v(-23.5, 2) * mm, "radius": 4 * mm});
            skPoint(sketch, "E59.centerSnap0", {"position": v(-40.5, 2) * mm});
            skPoint(sketch, "E59.centerSnap1", {"position": v(-23.5, -10) * mm});
            skCircle(sketch, "E60", {"center": v(-38, 9.5) * mm, "radius": 1.6 * mm});
            skCircle(sketch, "E61", {"center": v(-38, -5.5) * mm, "radius": 1.6 * mm});
            skCircle(sketch, "E62", {"center": v(-9, 9.5) * mm, "radius": 1.6 * mm});
            skCircle(sketch, "E63", {"center": v(-9, -5.5) * mm, "radius": 1.6 * mm});
            skCircle(sketch, "E64", {"center": v(-29, 7.5) * mm, "radius": 2.75 * mm});
            skCircle(sketch, "E65", {"center": v(-18, 7.5) * mm, "radius": 2.75 * mm});
            skCircle(sketch, "E66", {"center": v(-29, -3.5) * mm, "radius": 2.75 * mm});
            skCircle(sketch, "E67", {"center": v(-18, -3.5) * mm, "radius": 2.75 * mm});
            skSolve(sketch);
        }
        {
            var Q0;
            Q0 = qSketchRegion(id + "F34", true);
            extrude(context, id + "F35", {"entities" : qUnion([Q0]), "operationType" : NewBodyOperationType.REMOVE, "oppositeDirection" : true, "depth" : 25 * mm, "offsetDistance" : 25 * mm});
        }
        {
            var Q0;
            Q0=makeQuery(id+"F22.opExtrude","SWEPT_FACE",FACE,{"disambiguationData":[OSD([sQuery(id+"F21.wireOp",EDGE,"E52.top")])]});
            var sketch = newSketch(context, id + "F36", { "sketchPlane" : qUnion([Q0])});
            skCircle(sketch, "E68", {"center": v(-38, 9.5) * mm, "radius": 1.2 * mm});
            skCircle(sketch, "E69.0", {"center": v(-23.5, 2) * mm, "radius": 4 * mm, "construction": true});
            skCircle(sketch, "E70", {"center": v(-38, -5.5) * mm, "radius": 1.2 * mm});
            skCircle(sketch, "E71", {"center": v(-9, 9.5) * mm, "radius": 1.2 * mm});
            skCircle(sketch, "E72", {"center": v(-9, -5.5) * mm, "radius": 1.2 * mm});
            skSolve(sketch);
        }
        {
            var Q0;
            Q0 = qSketchRegion(id + "F36", true);
            extrude(context, id + "F37", {"entities" : qUnion([Q0]), "operationType" : NewBodyOperationType.REMOVE, "oppositeDirection" : true, "depth" : 8 * mm, "offsetDistance" : 25 * mm});
        }
        {
            var Q0;
            Q0=makeQuery(id+"F22.boolean.opBoolean","SPLIT",FACE,{"disambiguationData":[TD([makeQuery(id+"F1.opExtrude","SWEPT_FACE",FACE,{"disambiguationData":[OSD([sQuery(id+"F0.wireOp",EDGE,"E19")])]})])],"derivedFrom":makeQuery(id+"F22.opExtrude","SWEPT_FACE",FACE,{"disambiguationData":[OSD([sQuery(id+"F21.wireOp",EDGE,"E52.bottom")])]})});
            var Q1;
            Q1=makeQuery(id+"F22.boolean.opBoolean","SPLIT",FACE,{"disambiguationData":[TD([makeQuery(id+"F1.opExtrude","SWEPT_FACE",FACE,{"disambiguationData":[OSD([sQuery(id+"F0.wireOp",EDGE,"E16")])]})])],"derivedFrom":makeQuery(id+"F22.opExtrude","SWEPT_FACE",FACE,{"disambiguationData":[OSD([sQuery(id+"F21.wireOp",EDGE,"E52.bottom")])]})});
            var Q2;
            Q2=makeQuery(id+"F22.boolean.opBoolean","SPLIT",FACE,{"disambiguationData":[TD([makeQuery(id+"F1.opExtrude","SWEPT_FACE",FACE,{"disambiguationData":[OSD([sQuery(id+"F0.wireOp",EDGE,"E20")])]})])],"derivedFrom":makeQuery(id+"F22.opExtrude","SWEPT_FACE",FACE,{"disambiguationData":[OSD([sQuery(id+"F21.wireOp",EDGE,"E52.bottom")])]})});
            extrude(context, id + "F38", {"entities" : qUnion([Q0, Q1, Q2]), "operationType" : NewBodyOperationType.REMOVE, "oppositeDirection" : true, "depth" : 25 * mm, "offsetDistance" : 25 * mm});
        }
    });
